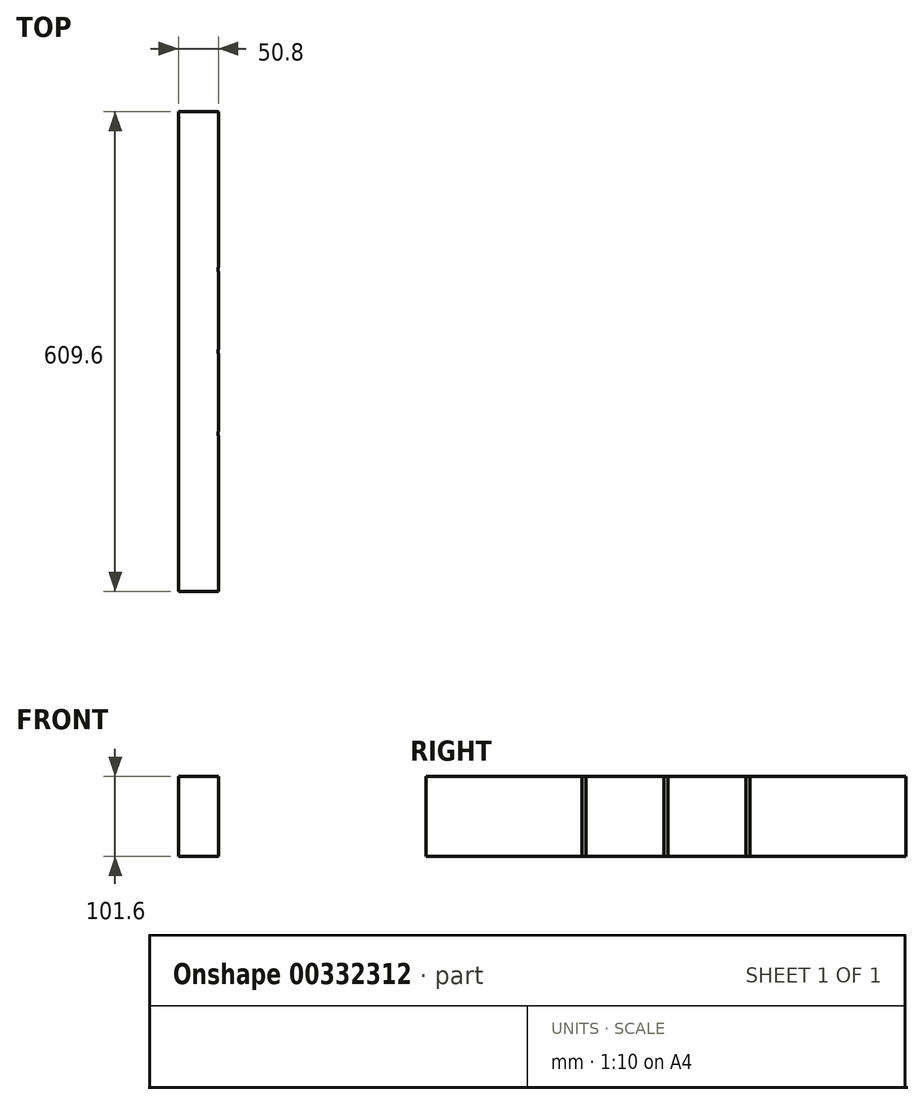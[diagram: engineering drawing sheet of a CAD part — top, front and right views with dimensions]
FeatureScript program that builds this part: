
annotation { "Feature Type Name" : "Feature", "Feature Type Description" : "" }
export const myFeature = defineFeature(function(context is Context, id is Id, definition is map)
    precondition{}
    {
        {
            var Q0;
            Q0=qCreatedBy(makeId("Right.planeOp"),FACE);
            var sketch = newSketch(context, id + "F0", { "sketchPlane" : qUnion([Q0])});
            skLineSegment(sketch, "E0.bottom", {"start": v(-35.7, 37.38) * mm, "end": v(573.9, 37.38) * mm});
            skLineSegment(sketch, "E0.top", {"start": v(-35.7, -64.22) * mm, "end": v(573.9, -64.22) * mm});
            skLineSegment(sketch, "E0.left", {"start": v(-35.7, 37.38) * mm, "end": v(-35.7, -64.22) * mm});
            skLineSegment(sketch, "E0.right", {"start": v(573.9, 37.38) * mm, "end": v(573.9, -64.22) * mm});
            skLineSegment(sketch, "E1", {"start": v(-35.7, -13.42) * mm, "end": v(269.1, -13.42) * mm});
            skLineSegment(sketch, "E2", {"start": v(269.1, -13.42) * mm, "end": v(269.1, 37.38) * mm});
            skLineSegment(sketch, "E3", {"start": v(269.1, -13.42) * mm, "end": v(269.1, -64.22) * mm});
            skSolve(sketch);
        }
        {
            var Q0;
            Q0 = qSketchRegion(id + "F0", true);
            extrude(context, id + "F1", {"entities" : qUnion([Q0]), "depth" : 50.8 * mm});
        }
        {
            var Q0;
            Q0=makeQuery(id+"F1.opExtrude","CAP_FACE",FACE,{"disambiguationData":[OSD([sQuery(id+"F0.wireOp",EDGE,"E0.bottom"),sQuery(id+"F0.wireOp",EDGE,"E0.top"),sQuery(id+"F0.wireOp",EDGE,"E0.left"),sQuery(id+"F0.wireOp",EDGE,"E0.right")])],"isStart":false});
            var sketch = newSketch(context, id + "F2", { "sketchPlane" : qUnion([Q0])});
            skLineSegment(sketch, "E4", {"start": v(-35.7, -13.42) * mm, "end": v(573.9, -13.42) * mm, "construction": true});
            skPoint(sketch, "E5.end.orphan", {"position": v(269.1, -64.22) * mm});
            skPoint(sketch, "E6.orphan", {"position": v(269.1, -13.42) * mm});
            skPoint(sketch, "E7.end.orphan", {"position": v(269.1, 37.38) * mm});
            skLineSegment(sketch, "E8", {"start": v(269.1, 37.38) * mm, "end": v(269.1, -64.22) * mm, "construction": true});
            skLineSegment(sketch, "E9", {"start": v(266.56, 24.68) * mm, "end": v(266.56, -64.22) * mm});
            skLineSegment(sketch, "E10", {"start": v(266.56, 24.68) * mm, "end": v(266.56, 37.38) * mm});
            skLineSegment(sketch, "E11", {"start": v(271.64, 24.68) * mm, "end": v(271.64, -64.22) * mm});
            skLineSegment(sketch, "E12", {"start": v(271.64, 24.68) * mm, "end": v(271.64, 37.38) * mm});
            skLineSegment(sketch, "E13", {"start": v(271.64, 37.38) * mm, "end": v(266.56, 37.38) * mm});
            skLineSegment(sketch, "E14", {"start": v(266.56, -64.22) * mm, "end": v(271.64, -64.22) * mm});
            skPoint(sketch, "E15.end.orphan", {"position": v(238.4, 24.68) * mm});
            skLineSegment(sketch, "E16", {"start": v(266.56, 24.68) * mm, "end": v(167.5, 24.68) * mm, "construction": true});
            skLineSegment(sketch, "E17", {"start": v(167.5, -56.28) * mm, "end": v(167.5, -64.22) * mm});
            skLineSegment(sketch, "E18", {"start": v(162.42, -56.28) * mm, "end": v(162.42, -64.22) * mm});
            skLineSegment(sketch, "E19", {"start": v(162.42, -64.22) * mm, "end": v(167.5, -64.22) * mm});
            skLineSegment(sketch, "E20", {"start": v(167.5, -56.28) * mm, "end": v(167.5, 37.38) * mm});
            skLineSegment(sketch, "E21", {"start": v(162.42, -56.28) * mm, "end": v(162.42, 37.38) * mm});
            skLineSegment(sketch, "E22", {"start": v(162.42, 37.38) * mm, "end": v(167.5, 37.38) * mm});
            skLineSegment(sketch, "E23", {"start": v(271.64, 24.68) * mm, "end": v(370.7, 24.68) * mm, "construction": true});
            skLineSegment(sketch, "E24", {"start": v(370.7, -55.82) * mm, "end": v(375.78, -55.82) * mm, "construction": true});
            skLineSegment(sketch, "E25", {"start": v(370.7, -55.82) * mm, "end": v(370.7, -64.22) * mm});
            skLineSegment(sketch, "E26", {"start": v(375.78, -55.82) * mm, "end": v(375.78, -64.22) * mm});
            skLineSegment(sketch, "E27", {"start": v(375.78, -64.22) * mm, "end": v(370.7, -64.22) * mm});
            skLineSegment(sketch, "E28", {"start": v(370.7, -55.82) * mm, "end": v(370.7, 37.38) * mm});
            skLineSegment(sketch, "E29", {"start": v(375.78, -55.82) * mm, "end": v(375.78, 37.38) * mm});
            skLineSegment(sketch, "E30", {"start": v(375.78, 37.38) * mm, "end": v(370.7, 37.38) * mm});
            skSolve(sketch);
        }
        {
            var Q0;
            Q0 = qSketchRegion(id + "F2", true);
            extrude(context, id + "F3", {"entities" : qUnion([Q0]), "operationType" : NewBodyOperationType.REMOVE, "oppositeDirection" : true, "depth" : 0.64 * mm});
        }
    });
